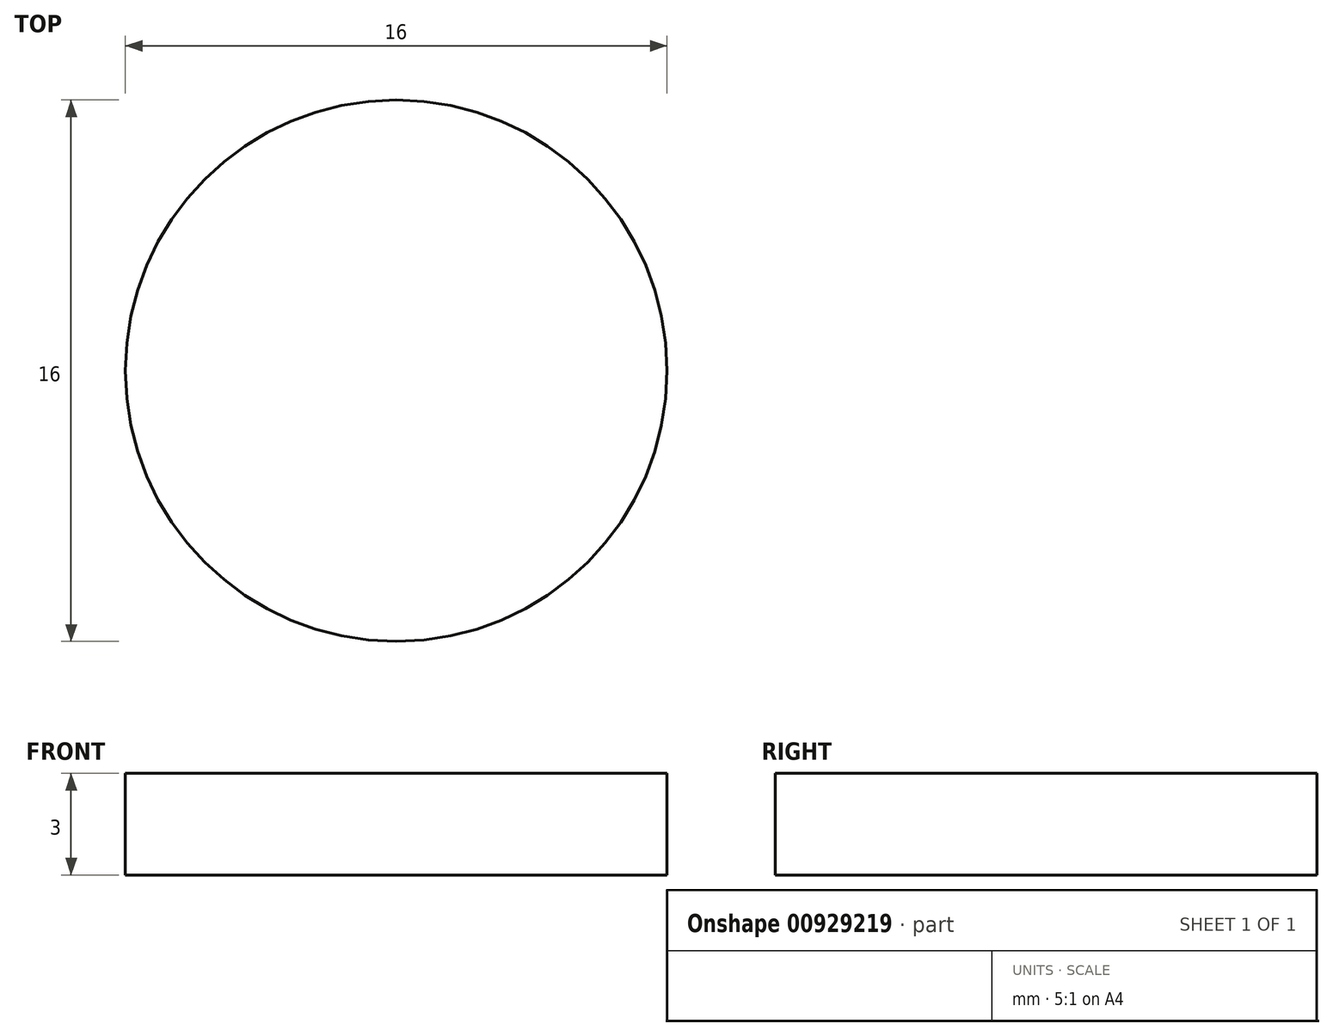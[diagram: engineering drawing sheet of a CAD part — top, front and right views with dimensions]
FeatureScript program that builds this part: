
annotation { "Feature Type Name" : "Feature", "Feature Type Description" : "" }
export const myFeature = defineFeature(function(context is Context, id is Id, definition is map)
    precondition{}
    {
        {
            var Q0;
            Q0=qCreatedBy(makeId("Top.planeOp"),FACE);
            var sketch = newSketch(context, id + "F0", { "sketchPlane" : qUnion([Q0])});
            skCircle(sketch, "E0", {"center": v(0, 0) * mm, "radius": 8 * mm});
            skSolve(sketch);
        }
        {
            var Q0;
            Q0=makeQuery(id+"F0.imprint","IMPRINT",FACE,{"disambiguationData":[TD([[makeQuery(id+"F0.imprint","IMPRINT",EDGE,{"derivedFrom":sQuery(id+"F0.wireOp",EDGE,"E0")}),1.0]])]});
            extrude(context, id + "F1", {"entities" : qUnion([Q0]), "depth" : 3 * mm, "offsetDistance" : 25 * mm});
        }
    });
